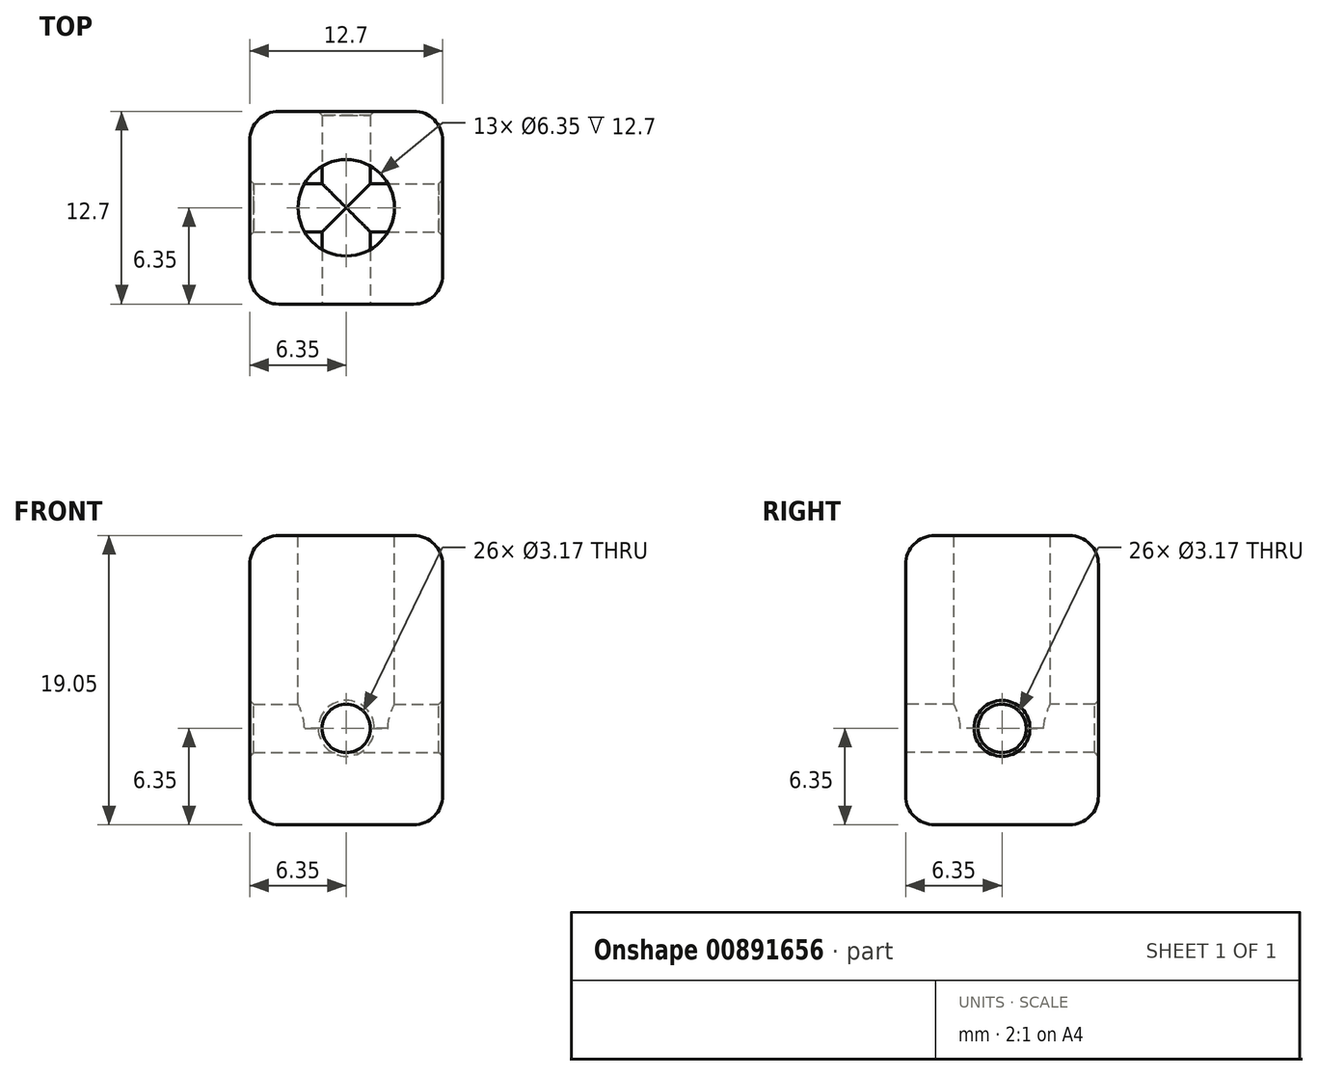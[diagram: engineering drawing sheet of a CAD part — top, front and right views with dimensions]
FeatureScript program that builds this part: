
annotation { "Feature Type Name" : "Feature", "Feature Type Description" : "" }
export const myFeature = defineFeature(function(context is Context, id is Id, definition is map)
    precondition{}
    {
        {
            var Q0;
            Q0=qCreatedBy(makeId("Top.planeOp"),FACE);
            var sketch = newSketch(context, id + "F0", { "sketchPlane" : qUnion([Q0])});
            skLineSegment(sketch, "E0.bottom", {"start": v(6.35, 6.35) * mm, "end": v(-6.35, 6.35) * mm});
            skLineSegment(sketch, "E0.top", {"start": v(6.35, -6.35) * mm, "end": v(-6.35, -6.35) * mm});
            skLineSegment(sketch, "E0.left", {"start": v(6.35, 6.35) * mm, "end": v(6.35, -6.35) * mm});
            skLineSegment(sketch, "E0.right", {"start": v(-6.35, 6.35) * mm, "end": v(-6.35, -6.35) * mm});
            skPoint(sketch, "E0.middle", {"position": v(0, 0) * mm});
            skSolve(sketch);
        }
        {
            var Q0;
            Q0 = qSketchRegion(id + "F0", true);
            extrude(context, id + "F1", {"entities" : qUnion([Q0]), "depth" : 19.05 * mm, "offsetDistance" : 25.4 * mm});
        }
        {
            var Q0;
            Q0=makeQuery(id+"F1.opExtrude","SWEPT_FACE",FACE,{"disambiguationData":[OSD([sQuery(id+"F0.wireOp",EDGE,"E0.top")])]});
            var sketch = newSketch(context, id + "F2", { "sketchPlane" : qUnion([Q0])});
            skCircle(sketch, "E1", {"center": v(0, 6.35) * mm, "radius": 1.59 * mm});
            skSolve(sketch);
        }
        {
            var Q0;
            Q0 = qSketchRegion(id + "F2", true);
            extrude(context, id + "F3", {"entities" : qUnion([Q0]), "operationType" : NewBodyOperationType.REMOVE, "oppositeDirection" : true, "depth" : 25.4 * mm, "offsetDistance" : 25.4 * mm});
        }
        {
            var Q0;
            Q0=qCreatedBy(makeId("Right.planeOp"),FACE);
            var sketch = newSketch(context, id + "F4", { "sketchPlane" : qUnion([Q0])});
            skCircle(sketch, "E2", {"center": v(0, 6.35) * mm, "radius": 1.59 * mm});
            skSolve(sketch);
        }
        {
            var Q0;
            Q0 = qSketchRegion(id + "F4", true);
            extrude(context, id + "F5", {"entities" : qUnion([Q0]), "operationType" : NewBodyOperationType.REMOVE, "endBound" : BoundingType.THROUGH_ALL, "oppositeDirection" : true, "depth" : 12.7 * mm, "offsetDistance" : 25.4 * mm, "hasSecondDirection" : true, "secondDirectionBound" : SecondDirectionBoundingType.THROUGH_ALL, "secondDirectionOppositeDirection" : false, "secondDirectionDepth" : 25.4 * mm});
        }
        {
            var Q0;
            Q0=makeQuery(id+"F1.opExtrude","CAP_FACE",FACE,{"disambiguationData":[OSD([sQuery(id+"F0.wireOp",EDGE,"E0.bottom"),sQuery(id+"F0.wireOp",EDGE,"E0.top"),sQuery(id+"F0.wireOp",EDGE,"E0.left"),sQuery(id+"F0.wireOp",EDGE,"E0.right")])],"isStart":false});
            var sketch = newSketch(context, id + "F6", { "sketchPlane" : qUnion([Q0])});
            skCircle(sketch, "E3", {"center": v(0, 0) * mm, "radius": 3.18 * mm});
            skSolve(sketch);
        }
        {
            var Q0;
            Q0=makeQuery(id+"F6.imprint","IMPRINT",FACE,{"disambiguationData":[TD([[makeQuery(id+"F6.imprint","IMPRINT",EDGE,{"derivedFrom":sQuery(id+"F6.wireOp",EDGE,"E3")}),1.0]])]});
            extrude(context, id + "F7", {"entities" : qUnion([Q0]), "operationType" : NewBodyOperationType.REMOVE, "oppositeDirection" : true, "depth" : 12.7 * mm, "offsetDistance" : 25.4 * mm});
        }
        {
            var Q0;
            Q0=makeQuery(id+"F1.opExtrude","CAP_EDGE",EDGE,{"disambiguationData":[OSD([sQuery(id+"F0.wireOp",EDGE,"E0.right")])],"isStart":false});
            var Q1;
            Q1=makeQuery(id+"F1.opExtrude","CAP_EDGE",EDGE,{"disambiguationData":[OSD([sQuery(id+"F0.wireOp",EDGE,"E0.top")])],"isStart":false});
            var Q2;
            Q2=makeQuery(id+"F1.opExtrude","CAP_EDGE",EDGE,{"disambiguationData":[OSD([sQuery(id+"F0.wireOp",EDGE,"E0.left")])],"isStart":false});
            var Q3;
            Q3=makeQuery(id+"F1.opExtrude","CAP_EDGE",EDGE,{"disambiguationData":[OSD([sQuery(id+"F0.wireOp",EDGE,"E0.bottom")])],"isStart":false});
            var Q4;
            Q4=makeQuery(id+"F1.opExtrude","SWEPT_EDGE",EDGE,{"disambiguationData":[OSD([sQuery(id+"F0.wireOp",EDGE,"E0.top"),sQuery(id+"F0.wireOp",EDGE,"E0.left")])]});
            var Q5;
            Q5=makeQuery(id+"F1.opExtrude","SWEPT_EDGE",EDGE,{"disambiguationData":[OSD([sQuery(id+"F0.wireOp",EDGE,"E0.bottom"),sQuery(id+"F0.wireOp",EDGE,"E0.left")])]});
            var Q6;
            Q6=makeQuery(id+"F1.opExtrude","SWEPT_EDGE",EDGE,{"disambiguationData":[OSD([sQuery(id+"F0.wireOp",EDGE,"E0.top"),sQuery(id+"F0.wireOp",EDGE,"E0.right")])]});
            var Q7;
            Q7=makeQuery(id+"F1.opExtrude","SWEPT_EDGE",EDGE,{"disambiguationData":[OSD([sQuery(id+"F0.wireOp",EDGE,"E0.bottom"),sQuery(id+"F0.wireOp",EDGE,"E0.right")])]});
            var Q8;
            Q8=makeQuery(id+"F1.opExtrude","CAP_EDGE",EDGE,{"disambiguationData":[OSD([sQuery(id+"F0.wireOp",EDGE,"E0.right")])],"isStart":true});
            var Q9;
            Q9=makeQuery(id+"F1.opExtrude","CAP_EDGE",EDGE,{"disambiguationData":[OSD([sQuery(id+"F0.wireOp",EDGE,"E0.top")])],"isStart":true});
            var Q10;
            Q10=makeQuery(id+"F1.opExtrude","CAP_EDGE",EDGE,{"disambiguationData":[OSD([sQuery(id+"F0.wireOp",EDGE,"E0.left")])],"isStart":true});
            var Q11;
            Q11=makeQuery(id+"F1.opExtrude","CAP_EDGE",EDGE,{"disambiguationData":[OSD([sQuery(id+"F0.wireOp",EDGE,"E0.bottom")])],"isStart":true});
            fillet(context, id + "F8", {"entities" : qUnion([Q0, Q1, Q2, Q3, Q4, Q5, Q6, Q7, Q8, Q9, Q10, Q11]), "radius" : 1.9 * mm, "tangentPropagation" : true, "allowEdgeOverflow" : false});
        }
        {
            var Q0;
            Q0=makeQuery(id+"F5.boolean.opBoolean","INTERSECT",EDGE,{"derivedFrom":[makeQuery(id+"F1.opExtrude","SWEPT_FACE",FACE,{"disambiguationData":[OSD([sQuery(id+"F0.wireOp",EDGE,"E0.left")])]}),makeQuery(id+"F5.opExtrude","SWEPT_FACE",FACE,{"disambiguationData":[OSD([sQuery(id+"F4.wireOp",EDGE,"E2")])]})]});
            var Q1;
            Q1=makeQuery(id+"F7.boolean.opBoolean","COPY",EDGE,{"derivedFrom":makeQuery(id+"F7.opExtrude","CAP_EDGE",EDGE,{"disambiguationData":[OSD([sQuery(id+"F6.wireOp",EDGE,"E3")])],"isStart":true})});
            var Q2;
            Q2=makeQuery(id+"F3.boolean.opBoolean","INTERSECT",EDGE,{"derivedFrom":[makeQuery(id+"F1.opExtrude","SWEPT_FACE",FACE,{"disambiguationData":[OSD([sQuery(id+"F0.wireOp",EDGE,"E0.bottom")])]}),makeQuery(id+"F3.opExtrude","SWEPT_FACE",FACE,{"disambiguationData":[OSD([sQuery(id+"F2.wireOp",EDGE,"E1")])]})]});
            var Q3;
            Q3=makeQuery(id+"F5.boolean.opBoolean","INTERSECT",EDGE,{"derivedFrom":[makeQuery(id+"F1.opExtrude","SWEPT_FACE",FACE,{"disambiguationData":[OSD([sQuery(id+"F0.wireOp",EDGE,"E0.right")])]}),makeQuery(id+"F5.opExtrude","SWEPT_FACE",FACE,{"disambiguationData":[OSD([sQuery(id+"F4.wireOp",EDGE,"E2")])]})]});
            var Q4;
            Q4=makeQuery(id+"F3.boolean.opBoolean","COPY",EDGE,{"derivedFrom":makeQuery(id+"F3.opExtrude","CAP_EDGE",EDGE,{"disambiguationData":[OSD([sQuery(id+"F2.wireOp",EDGE,"E1")])],"isStart":true})});
            chamfer(context, id + "F9", {"entities" : qUnion([Q0, Q1, Q2, Q3, Q4]), "width" : 0.25 * mm, "tangentPropagation" : true});
        }
    });
